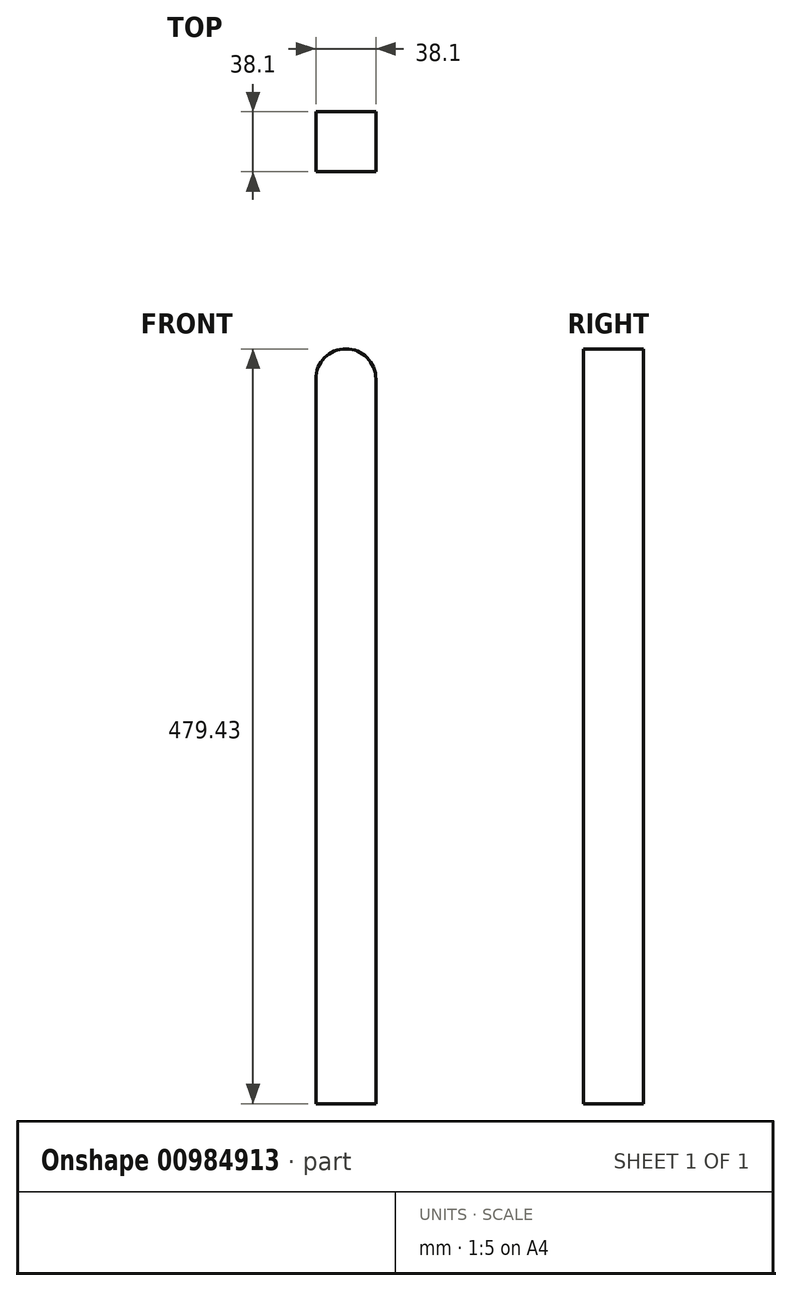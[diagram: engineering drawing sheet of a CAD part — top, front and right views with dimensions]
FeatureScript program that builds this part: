
annotation { "Feature Type Name" : "Feature", "Feature Type Description" : "" }
export const myFeature = defineFeature(function(context is Context, id is Id, definition is map)
    precondition{}
    {
        {
            var Q0;
            Q0=qCreatedBy(makeId("Front.planeOp"),FACE);
            var sketch = newSketch(context, id + "F0", { "sketchPlane" : qUnion([Q0])});
            skLineSegment(sketch, "E0.bottom", {"start": v(0, 0) * mm, "end": v(-38.1, 0) * mm});
            skLineSegment(sketch, "E0.top", {"start": v(-19.05, 479.43) * mm, "end": v(-19.05, 479.43) * mm});
            skLineSegment(sketch, "E0.left", {"start": v(0, 0) * mm, "end": v(0, 460.38) * mm});
            skLineSegment(sketch, "E0.right", {"start": v(-38.1, 0) * mm, "end": v(-38.1, 460.38) * mm});
            skPoint(sketch, "E1.visualSharp", {"position": v(-38.1, 479.43) * mm});
            skArc(sketch, "E1.filletArc", {"start": v(-19.05, 479.43) * mm, "mid": v(-32.52, 473.85) * mm, "end": v(-38.1, 460.38) * mm});
            skPoint(sketch, "E2.visualSharp", {"position": v(0, 479.43) * mm});
            skArc(sketch, "E2.filletArc", {"start": v(0, 460.38) * mm, "mid": v(-5.58, 473.85) * mm, "end": v(-19.05, 479.43) * mm});
            skSolve(sketch);
        }
        {
            var Q0;
            Q0 = qSketchRegion(id + "F0", true);
            extrude(context, id + "F1", {"entities" : qUnion([Q0]), "depth" : 38.1 * mm, "offsetDistance" : 25.4 * mm});
        }
    });
